# Revit family: Legrand-Ups-Keor_T_EVO-10_20kVA
name_source: partatom
category: Installations électriques
revit_build: Autodesk Revit 2018 (Build: 20170223_1515(x64)
units: mm (PartAtom-declared; Revit-internal decimal feet)

## family parameters
Basée sur le plan de construction = Non
Conserver l'orientation des annotations = Non
Cote de connecteur circulaire = Utiliser le diamètre
Couper avec des vides une fois chargée = Non
Numéro OmniClass = 23.80.10.17.34
Partagée = Non
Point de calcul de pièce = Non
Titre OmniClass = Static Uninterruptible Power Supplies
Toujours verticalement = Oui
Type d'élément = Normal

## types (8) — shared parameters
Back Clearance = 250 mm  [stored 0.82021 ft]
Cabinet Depth = 800 mm  [stored 2.62467 ft]
Cabinet Height = 1020 mm  [stored 3.34646 ft]
Cabinet Width = 265 mm  [stored 0.869423 ft]
Conductors = Cables
Connection constraint = Behind and Bottom
Connection constraint (signal) = Ahead and above/bottom
Fabricant = LEGRAND
Frequency of use = 50 Hz or 60 Hz selectable
Front Clearance = 900 mm  [stored 2.95276 ft]
General Conditions of Use = https://export.legrand.com
Humidity = 20-95% not condensing
Input / Output phase configuration = 3ph+N+PE / 3ph+N+PE
Installation space = 0.2 m³
Installation type = On the floor
Max sound pressure level = < 51 dB at 1m
Modèle = KEOR T EVO
Operating altitude = up to 1000 m altitude without derating
Operating temperature = from 0°C to +40°C
Output Voltage = 380,400,415 Vac
Output power factor = 1
Side Clearance = 120 mm  [stored 0.393701 ft]
URL = https://ups.legrand.com
Visibilità aree d'installazione = Oui

## per-type parameters (varying)
| type | Active power of use | Nominal Power | Weight |
| LG-310270 | 10 kW | 10 kVA | 78.0 kg |
| LG-310271 | 10 kW | 10 kVA | 145.0 kg |
| LG-310272 | 10 kW | 10 kVA | 168.0 kg |
| LG-310273 | 15 kW | 15 kVA | 79.0 kg |
| LG-310274 | 15 kW | 15 kVA | 163.0 kg |
| LG-310275 | 15 kW | 15 kVA | 180.0 kg |
| LG-310276 | 20 kW | 20 kVA | 84.0 kg |
| LG-310277 | 20 kW | 20 kVA | 185.0 kg |

note: [stored X ft] marks values corroborated as IEEE doubles in the binary element streams (Revit-internal decimal feet)
